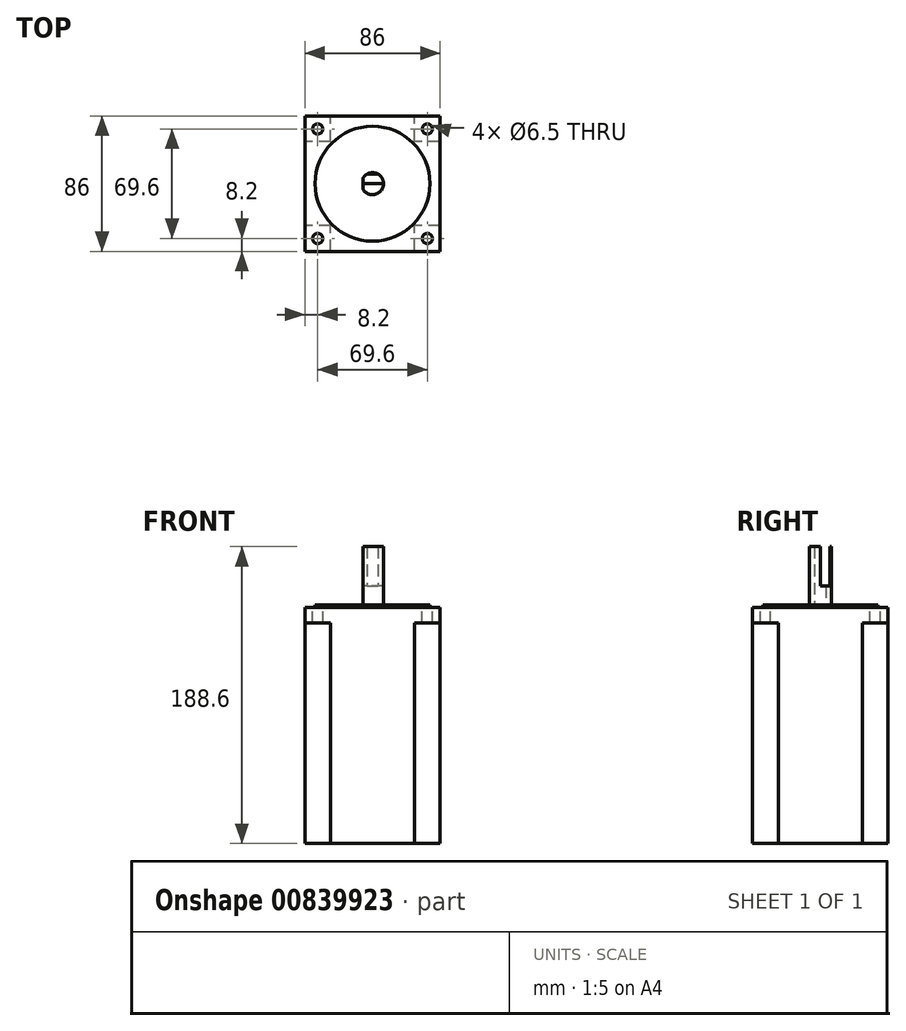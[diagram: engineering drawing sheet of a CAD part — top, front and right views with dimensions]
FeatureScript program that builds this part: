
annotation { "Feature Type Name" : "Feature", "Feature Type Description" : "" }
export const myFeature = defineFeature(function(context is Context, id is Id, definition is map)
    precondition{}
    {
        {
            var Q0;
            Q0=qCreatedBy(makeId("Top.planeOp"),FACE);
            var sketch = newSketch(context, id + "F0", { "sketchPlane" : qUnion([Q0])});
            skLineSegment(sketch, "E0.bottom", {"start": v(43, 43) * mm, "end": v(-43, 43) * mm});
            skLineSegment(sketch, "E0.top", {"start": v(43, -43) * mm, "end": v(-43, -43) * mm});
            skLineSegment(sketch, "E0.left", {"start": v(43, 43) * mm, "end": v(43, -43) * mm});
            skLineSegment(sketch, "E0.right", {"start": v(-43, 43) * mm, "end": v(-43, -43) * mm});
            skPoint(sketch, "E0.middle", {"position": v(0, 0) * mm});
            skSolve(sketch);
        }
        {
            var Q0;
            Q0 = qSketchRegion(id + "F0", true);
            extrude(context, id + "F1", {"entities" : qUnion([Q0]), "depth" : 150 * mm, "offsetDistance" : 25 * mm});
        }
        {
            var Q0;
            Q0=makeQuery(id+"F1.opExtrude","CAP_FACE",FACE,{"disambiguationData":[OSD([sQuery(id+"F0.wireOp",EDGE,"E0.bottom"),sQuery(id+"F0.wireOp",EDGE,"E0.top"),sQuery(id+"F0.wireOp",EDGE,"E0.left"),sQuery(id+"F0.wireOp",EDGE,"E0.right")])],"isStart":false});
            var sketch = newSketch(context, id + "F2", { "sketchPlane" : qUnion([Q0])});
            skLineSegment(sketch, "E1", {"start": v(-43, 34.8) * mm, "end": v(-33.5, 34.8) * mm});
            skLineSegment(sketch, "E2", {"start": v(-34.8, 43) * mm, "end": v(-34.8, 34.8) * mm});
            skLineSegment(sketch, "E3", {"start": v(-34.8, 34.8) * mm, "end": v(34.8, 34.8) * mm});
            skLineSegment(sketch, "E4", {"start": v(34.8, 34.8) * mm, "end": v(34.8, -34.8) * mm});
            skLineSegment(sketch, "E5", {"start": v(34.8, -34.8) * mm, "end": v(-34.8, -34.8) * mm});
            skSolve(sketch);
        }
        {
            var Q0;
            Q0=sQuery(id+"F2.wireOp",VERTEX,"E2.end");
            var Q1;
            Q1=sQuery(id+"F2.wireOp",VERTEX,"E3.end");
            var Q2;
            Q2=sQuery(id+"F2.wireOp",VERTEX,"E4.end");
            var Q3;
            Q3=sQuery(id+"F2.wireOp",VERTEX,"E5.end");
            var Q4;
            Q4=makeQuery(id+"F1.opExtrude","SWEPT_BODY",BODY,{"disambiguationData":[OSD([sQuery(id+"F0.wireOp",EDGE,"E0.bottom"),sQuery(id+"F0.wireOp",EDGE,"E0.top"),sQuery(id+"F0.wireOp",EDGE,"E0.left"),sQuery(id+"F0.wireOp",EDGE,"E0.right")])]});
            hole(context, id + "F3", {"style" : HoleStyle.SIMPLE, "endStyle" : HoleEndStyle.THROUGH, "holeDiameter" : 6.5 * mm, "majorDiameter" : 5 * mm, "isTappedThrough" : true, "tappedDepth" : 12 * mm, "tapClearance" : 3, "locations" : qUnion([Q0, Q1, Q2, Q3]), "scope" : qUnion([Q4])});
        }
        {
            var Q0;
            Q0=makeQuery(id+"F1.opExtrude","CAP_FACE",FACE,{"disambiguationData":[OSD([sQuery(id+"F0.wireOp",EDGE,"E0.bottom"),sQuery(id+"F0.wireOp",EDGE,"E0.top"),sQuery(id+"F0.wireOp",EDGE,"E0.left"),sQuery(id+"F0.wireOp",EDGE,"E0.right")])],"isStart":false});
            var sketch = newSketch(context, id + "F4", { "sketchPlane" : qUnion([Q0])});
            skCircle(sketch, "E6", {"center": v(0, 0) * mm, "radius": 36.5 * mm});
            skSolve(sketch);
        }
        {
            var Q0;
            Q0=makeQuery(id+"F4.imprint","IMPRINT",FACE,{"disambiguationData":[TD([[makeQuery(id+"F4.imprint","IMPRINT",EDGE,{"derivedFrom":sQuery(id+"F4.wireOp",EDGE,"E6")}),1.0]])]});
            extrude(context, id + "F5", {"entities" : qUnion([Q0]), "operationType" : NewBodyOperationType.ADD, "depth" : 1.6 * mm, "offsetDistance" : 25 * mm});
        }
        {
            var Q0;
            Q0=makeQuery(id+"F5.opExtrude","CAP_FACE",FACE,{"disambiguationData":[OSD([sQuery(id+"F4.wireOp",EDGE,"E6")])],"isStart":false});
            var sketch = newSketch(context, id + "F6", { "sketchPlane" : qUnion([Q0])});
            skCircle(sketch, "E7", {"center": v(0, 0) * mm, "radius": 7 * mm});
            skLineSegment(sketch, "E8", {"start": v(0, -7) * mm, "end": v(0, 6) * mm});
            skLineSegment(sketch, "E9", {"start": v(-8.6, 6) * mm, "end": v(8.82, 6) * mm});
            skLineSegment(sketch, "E10", {"start": v(7, 0) * mm, "end": v(-6, 0) * mm});
            skLineSegment(sketch, "E11", {"start": v(-6, 0) * mm, "end": v(-6, -7.03) * mm});
            skLineSegment(sketch, "E12", {"start": v(-6, -7.03) * mm, "end": v(-6, 6) * mm});
            skSolve(sketch);
        }
        {
            var Q0;
            {var subQ0=sQuery(id+"F6.wireOp",EDGE,"E9");var subQ1=sQuery(id+"F6.wireOp",EDGE,"E7");var subQ2=makeQuery(id+"F6.imprint","INTERSECT",VERTEX,{"disambiguationData":[OD(0.0)],"derivedFrom":[subQ1,subQ0]});Q0=makeQuery(id+"F6.imprint","IMPRINT",FACE,{"disambiguationData":[TD([[makeQuery(id+"F6.imprint","IMPRINT",EDGE,{"disambiguationData":[TD([[subQ2,-1.0]])],"derivedFrom":subQ1}),1.0]])]});}
            var Q1;
            {var subQ0=sQuery(id+"F6.wireOp",EDGE,"E12");var subQ1=sQuery(id+"F6.wireOp",EDGE,"E7");var subQ2=makeQuery(id+"F6.imprint","INTERSECT",VERTEX,{"disambiguationData":[OD(0.0)],"derivedFrom":[subQ1,subQ0]});Q1=makeQuery(id+"F6.imprint","IMPRINT",FACE,{"disambiguationData":[TD([[makeQuery(id+"F6.imprint","IMPRINT",EDGE,{"disambiguationData":[TD([[subQ2,1.0]])],"derivedFrom":subQ1}),1.0]])]});}
            var Q2;
            {var subQ0=sQuery(id+"F6.wireOp",EDGE,"E8");var subQ1=sQuery(id+"F6.wireOp",EDGE,"E7");var subQ2=makeQuery(id+"F6.imprint","INTERSECT",VERTEX,{"derivedFrom":[subQ1,subQ0]});Q2=makeQuery(id+"F6.imprint","IMPRINT",FACE,{"disambiguationData":[TD([[makeQuery(id+"F6.imprint","IMPRINT",EDGE,{"disambiguationData":[TD([[subQ2,-1.0]])],"derivedFrom":subQ1}),1.0]])]});}
            var Q3;
            {var subQ0=sQuery(id+"F6.wireOp",EDGE,"E10");var subQ1=sQuery(id+"F6.wireOp",EDGE,"E7");var subQ2=makeQuery(id+"F6.imprint","INTERSECT",VERTEX,{"derivedFrom":[subQ1,subQ0]});Q3=makeQuery(id+"F6.imprint","IMPRINT",FACE,{"disambiguationData":[TD([[makeQuery(id+"F6.imprint","IMPRINT",EDGE,{"disambiguationData":[TD([[subQ2,-1.0]])],"derivedFrom":subQ1}),1.0]])]});}
            var Q4;
            {var subQ0=sQuery(id+"F6.wireOp",EDGE,"E8");var subQ1=sQuery(id+"F6.wireOp",EDGE,"E7");var subQ2=makeQuery(id+"F6.imprint","INTERSECT",VERTEX,{"derivedFrom":[subQ1,subQ0]});Q4=makeQuery(id+"F6.imprint","IMPRINT",FACE,{"disambiguationData":[TD([[makeQuery(id+"F6.imprint","IMPRINT",EDGE,{"disambiguationData":[TD([[subQ2,1.0]])],"derivedFrom":subQ1}),1.0]])]});}
            var Q5;
            {var subQ0=sQuery(id+"F6.wireOp",EDGE,"E9");var subQ3=sQuery(id+"F6.wireOp",EDGE,"E7");var subQ4=makeQuery(id+"F6.imprint","INTERSECT",VERTEX,{"disambiguationData":[OD(1.0)],"derivedFrom":[subQ3,subQ0]});Q5=makeQuery(id+"F6.imprint","IMPRINT",FACE,{"disambiguationData":[TD([[makeQuery(id+"F6.imprint","IMPRINT",EDGE,{"disambiguationData":[TD([[subQ4,-1.0]])],"derivedFrom":subQ3}),1.0]])]});}
            extrude(context, id + "F7", {"entities" : qUnion([Q0, Q1, Q2, Q3, Q4, Q5]), "operationType" : NewBodyOperationType.ADD, "depth" : 12 * mm, "offsetDistance" : 25 * mm});
        }
        {
            var Q0;
            Q0=makeQuery(id+"F7.opExtrude","CAP_FACE",FACE,{"disambiguationData":[OSD([sQuery(id+"F6.wireOp",EDGE,"E7")])],"isStart":false});
            var sketch = newSketch(context, id + "F8", { "sketchPlane" : qUnion([Q0])});
            skCircle(sketch, "E13", {"center": v(0, 0) * mm, "radius": 7 * mm});
            skLineSegment(sketch, "E14", {"start": v(0, -7) * mm, "end": v(0, 6) * mm});
            skLineSegment(sketch, "E15", {"start": v(-3.6, 6) * mm, "end": v(3.6, 6) * mm});
            skLineSegment(sketch, "E16", {"start": v(7, 0) * mm, "end": v(-6, 0) * mm});
            skLineSegment(sketch, "E17", {"start": v(-6, 0) * mm, "end": v(-6, -3.6) * mm});
            skLineSegment(sketch, "E18", {"start": v(-6, -3.6) * mm, "end": v(-6, 3.6) * mm});
            skSolve(sketch);
        }
        {
            var Q0;
            {var subQ0=sQuery(id+"F8.wireOp",EDGE,"E14");var subQ1=sQuery(id+"F8.wireOp",EDGE,"E13");var subQ2=makeQuery(id+"F8.imprint","INTERSECT",VERTEX,{"derivedFrom":[subQ1,subQ0]});Q0=makeQuery(id+"F8.imprint","IMPRINT",FACE,{"disambiguationData":[TD([[makeQuery(id+"F8.imprint","IMPRINT",EDGE,{"disambiguationData":[TD([[subQ2,-1.0]])],"derivedFrom":subQ1}),1.0]])]});}
            var Q1;
            {var subQ0=sQuery(id+"F8.wireOp",EDGE,"E15");var subQ1=sQuery(id+"F8.wireOp",EDGE,"E13");var subQ2=makeQuery(id+"F8.imprint","INTERSECT",VERTEX,{"disambiguationData":[OD(1.0)],"derivedFrom":[subQ1,subQ0]});Q1=makeQuery(id+"F8.imprint","IMPRINT",FACE,{"disambiguationData":[TD([[makeQuery(id+"F8.imprint","IMPRINT",EDGE,{"disambiguationData":[TD([[subQ2,1.0]])],"derivedFrom":subQ1}),1.0]])]});}
            var Q2;
            {var subQ0=sQuery(id+"F8.wireOp",EDGE,"E14");var subQ1=sQuery(id+"F8.wireOp",EDGE,"E13");var subQ2=makeQuery(id+"F8.imprint","INTERSECT",VERTEX,{"derivedFrom":[subQ1,subQ0]});Q2=makeQuery(id+"F8.imprint","IMPRINT",FACE,{"disambiguationData":[TD([[makeQuery(id+"F8.imprint","IMPRINT",EDGE,{"disambiguationData":[TD([[subQ2,1.0]])],"derivedFrom":subQ1}),1.0]])]});}
            var Q3;
            {var subQ5=sQuery(id+"F8.wireOp",EDGE,"E15");var subQ7=sQuery(id+"F8.wireOp",EDGE,"E13");var subQ8=makeQuery(id+"F8.imprint","INTERSECT",VERTEX,{"disambiguationData":[OD(0.0)],"derivedFrom":[subQ7,subQ5]});Q3=makeQuery(id+"F8.imprint","IMPRINT",FACE,{"disambiguationData":[TD([[makeQuery(id+"F8.imprint","IMPRINT",EDGE,{"disambiguationData":[TD([[subQ8,-1.0]])],"derivedFrom":subQ7}),1.0]])]});}
            extrude(context, id + "F9", {"entities" : qUnion([Q0, Q1, Q2, Q3]), "operationType" : NewBodyOperationType.ADD, "depth" : 25 * mm, "offsetDistance" : 25 * mm});
        }
        {
            var Q0;
            Q0=makeQuery(id+"F1.opExtrude","CAP_FACE",FACE,{"disambiguationData":[OSD([sQuery(id+"F0.wireOp",EDGE,"E0.bottom"),sQuery(id+"F0.wireOp",EDGE,"E0.top"),sQuery(id+"F0.wireOp",EDGE,"E0.left"),sQuery(id+"F0.wireOp",EDGE,"E0.right")])],"isStart":true});
            var sketch = newSketch(context, id + "F10", { "sketchPlane" : qUnion([Q0])});
            skLineSegment(sketch, "E19.bottom", {"start": v(-26.6, -26.6) * mm, "end": v(-43, -26.6) * mm});
            skLineSegment(sketch, "E19.top", {"start": v(-26.6, -43) * mm, "end": v(-43, -43) * mm});
            skLineSegment(sketch, "E19.left", {"start": v(-26.6, -26.6) * mm, "end": v(-26.6, -43) * mm});
            skLineSegment(sketch, "E19.right", {"start": v(-43, -26.6) * mm, "end": v(-43, -43) * mm});
            skPoint(sketch, "E19.middle", {"position": v(-34.8, -34.8) * mm});
            skLineSegment(sketch, "E20.bottom", {"start": v(-26.6, 43) * mm, "end": v(-43, 43) * mm});
            skLineSegment(sketch, "E20.top", {"start": v(-26.6, 26.6) * mm, "end": v(-43, 26.6) * mm});
            skLineSegment(sketch, "E20.left", {"start": v(-26.6, 43) * mm, "end": v(-26.6, 26.6) * mm});
            skLineSegment(sketch, "E20.right", {"start": v(-43, 43) * mm, "end": v(-43, 26.6) * mm});
            skPoint(sketch, "E20.middle", {"position": v(-34.8, 34.8) * mm});
            skLineSegment(sketch, "E21.bottom", {"start": v(43, 43) * mm, "end": v(26.6, 43) * mm});
            skLineSegment(sketch, "E21.top", {"start": v(43, 26.6) * mm, "end": v(26.6, 26.6) * mm});
            skLineSegment(sketch, "E21.left", {"start": v(43, 43) * mm, "end": v(43, 26.6) * mm});
            skLineSegment(sketch, "E21.right", {"start": v(26.6, 43) * mm, "end": v(26.6, 26.6) * mm});
            skPoint(sketch, "E21.middle", {"position": v(34.8, 34.8) * mm});
            skLineSegment(sketch, "E22.bottom", {"start": v(43, -26.6) * mm, "end": v(26.6, -26.6) * mm});
            skLineSegment(sketch, "E22.top", {"start": v(43, -43) * mm, "end": v(26.6, -43) * mm});
            skLineSegment(sketch, "E22.left", {"start": v(43, -26.6) * mm, "end": v(43, -43) * mm});
            skLineSegment(sketch, "E22.right", {"start": v(26.6, -26.6) * mm, "end": v(26.6, -43) * mm});
            skPoint(sketch, "E22.middle", {"position": v(34.8, -34.8) * mm});
            skSolve(sketch);
        }
        {
            var Q0;
            Q0=makeQuery(id+"F10.imprint","IMPRINT",FACE,{"disambiguationData":[TD([[makeQuery(id+"F10.imprint","IMPRINT",EDGE,{"derivedFrom":sQuery(id+"F10.wireOp",EDGE,"E20.bottom")}),1.0]])]});
            var Q1;
            Q1=makeQuery(id+"F10.imprint","IMPRINT",FACE,{"disambiguationData":[TD([[makeQuery(id+"F10.imprint","IMPRINT",EDGE,{"derivedFrom":sQuery(id+"F10.wireOp",EDGE,"E21.bottom")}),1.0]])]});
            var Q2;
            Q2=makeQuery(id+"F10.imprint","IMPRINT",FACE,{"disambiguationData":[TD([[makeQuery(id+"F10.imprint","IMPRINT",EDGE,{"derivedFrom":sQuery(id+"F10.wireOp",EDGE,"E22.bottom")}),1.0]])]});
            var Q3;
            Q3=makeQuery(id+"F10.imprint","IMPRINT",FACE,{"disambiguationData":[TD([[makeQuery(id+"F10.imprint","IMPRINT",EDGE,{"derivedFrom":sQuery(id+"F10.wireOp",EDGE,"E19.bottom")}),1.0]])]});
            extrude(context, id + "F11", {"entities" : qUnion([Q0, Q1, Q2, Q3]), "operationType" : NewBodyOperationType.REMOVE, "oppositeDirection" : true, "depth" : 140 * mm, "offsetDistance" : 25 * mm});
        }
    });
